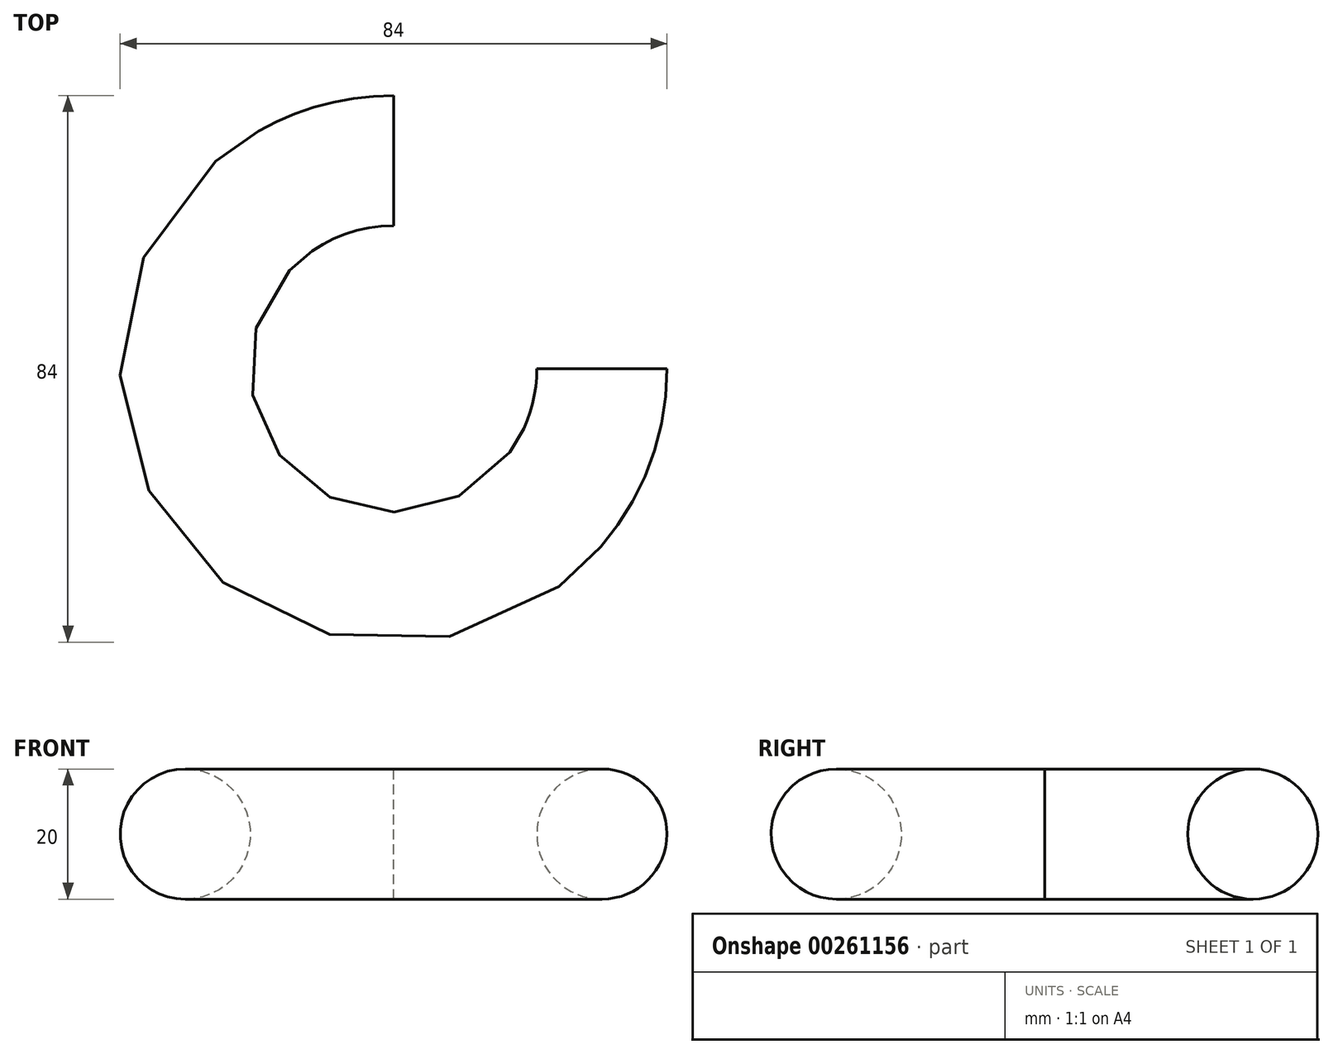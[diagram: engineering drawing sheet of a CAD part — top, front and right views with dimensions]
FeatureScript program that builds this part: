
annotation { "Feature Type Name" : "Feature", "Feature Type Description" : "" }
export const myFeature = defineFeature(function(context is Context, id is Id, definition is map)
    precondition{}
    {
        {
            var Q0;
            Q0=qCreatedBy(makeId("Front.planeOp"),FACE);
            var sketch = newSketch(context, id + "F0", { "sketchPlane" : qUnion([Q0])});
            skCircle(sketch, "E0", {"center": v(32, 0) * mm, "radius": 10 * mm});
            skLineSegment(sketch, "E1", {"start": v(0, 45.18) * mm, "end": v(0, -53.8) * mm, "construction": true});
            skSolve(sketch);
        }
        {
            var Q0;
            Q0=makeQuery(id+"F0.imprint","IMPRINT",FACE,{"disambiguationData":[TD([[makeQuery(id+"F0.imprint","IMPRINT",EDGE,{"derivedFrom":sQuery(id+"F0.wireOp",EDGE,"E0")}),1.0]])]});
            var Q1;
            Q1=sQuery(id+"F0.wireOp",EDGE,"E1");
            var Q2;
            Q2=sQuery(id+"F0.wireOp",EDGE,"E1");
            revolve(context, id + "F1", {"entities" : qUnion([Q0]), "surfaceEntities" : qUnion([Q1]), "axis" : qUnion([Q2]), "revolveType" : RevolveType.ONE_DIRECTION, "angle" : 270 * degree});
        }
    });
